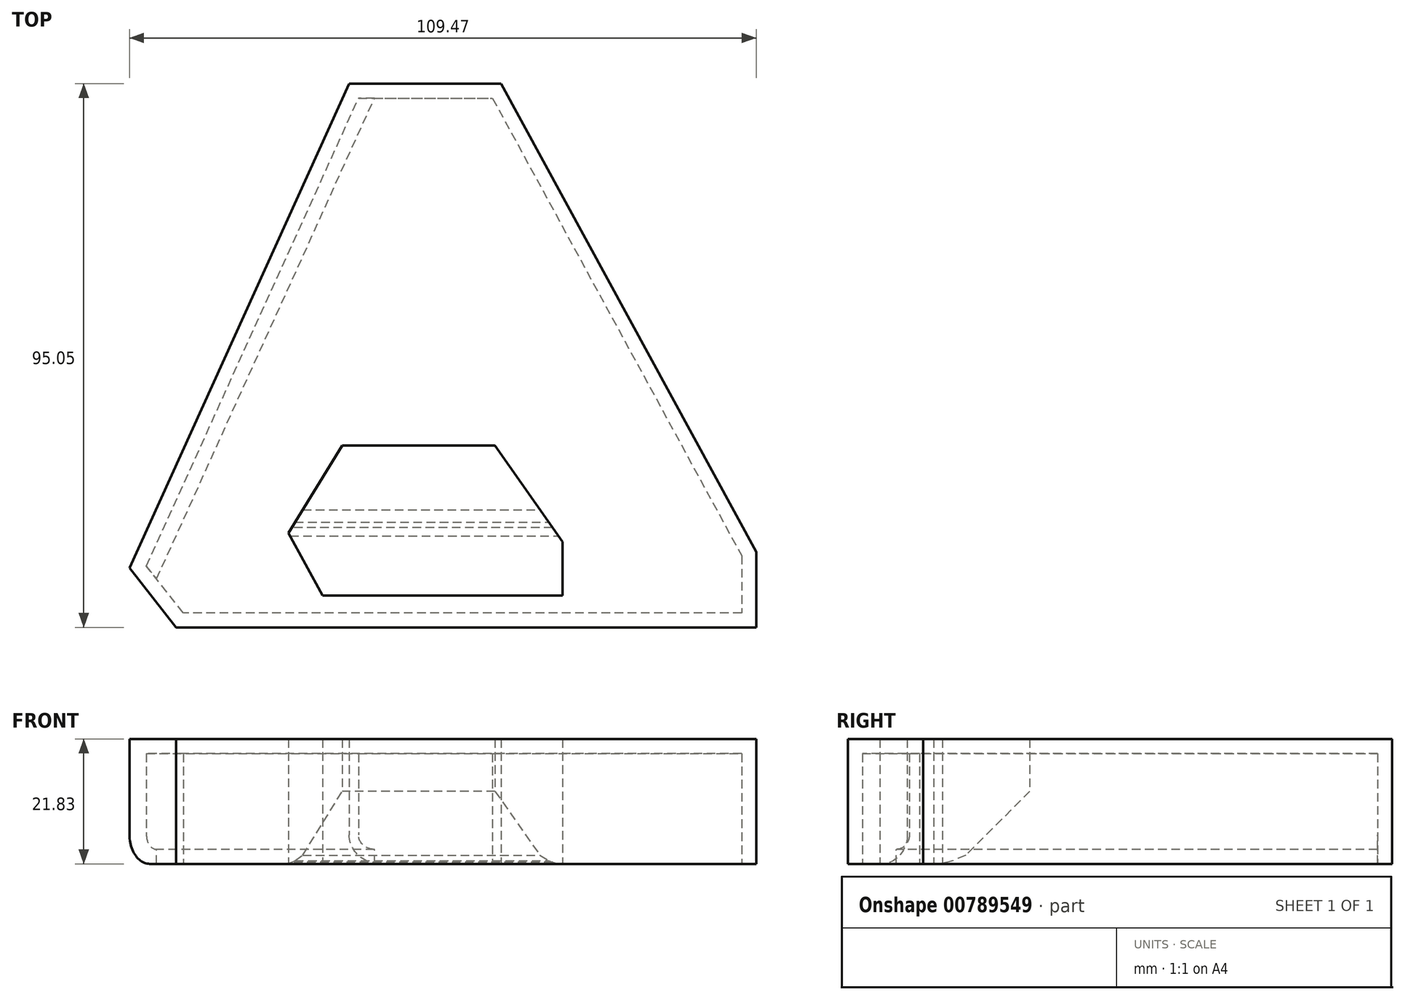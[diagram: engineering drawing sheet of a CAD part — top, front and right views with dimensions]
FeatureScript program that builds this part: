
annotation { "Feature Type Name" : "Feature", "Feature Type Description" : "" }
export const myFeature = defineFeature(function(context is Context, id is Id, definition is map)
    precondition{}
    {
        {
            var Q0;
            Q0=qCreatedBy(makeId("Top.planeOp"),FACE);
            var sketch = newSketch(context, id + "F0", { "sketchPlane" : qUnion([Q0])});
            skLineSegment(sketch, "E0", {"start": v(-11, 53.07) * mm, "end": v(15.55, 53.07) * mm});
            skLineSegment(sketch, "E1", {"start": v(15.55, 53.07) * mm, "end": v(60.1, -28.8) * mm});
            skLineSegment(sketch, "E2", {"start": v(60.1, -28.8) * mm, "end": v(60.1, -41.98) * mm});
            skLineSegment(sketch, "E3", {"start": v(60.1, -41.98) * mm, "end": v(-41.23, -41.98) * mm});
            skLineSegment(sketch, "E4", {"start": v(-41.23, -41.98) * mm, "end": v(-49.37, -31.59) * mm});
            skLineSegment(sketch, "E5", {"start": v(-49.37, -31.59) * mm, "end": v(-11, 53.07) * mm});
            skSolve(sketch);
        }
        {
            var Q0;
            Q0=qCreatedBy(makeId("Top.planeOp"),FACE);
            var sketch = newSketch(context, id + "F1", { "sketchPlane" : qUnion([Q0])});
            skLineSegment(sketch, "E6", {"start": v(-15.66, -36.38) * mm, "end": v(26.25, -36.38) * mm});
            skLineSegment(sketch, "E7", {"start": v(26.25, -36.38) * mm, "end": v(26.25, -26.99) * mm});
            skLineSegment(sketch, "E8", {"start": v(26.25, -26.99) * mm, "end": v(14.48, -10.19) * mm});
            skLineSegment(sketch, "E9", {"start": v(14.48, -10.19) * mm, "end": v(-12.2, -10.19) * mm});
            skLineSegment(sketch, "E10", {"start": v(-12.2, -10.19) * mm, "end": v(-21.63, -25.46) * mm});
            skLineSegment(sketch, "E11", {"start": v(-21.63, -25.46) * mm, "end": v(-15.66, -36.38) * mm});
            skSolve(sketch);
        }
        {
            var Q0;
            Q0=makeQuery(id+"F1.imprint","IMPRINT",FACE,{"disambiguationData":[TD([[makeQuery(id+"F1.imprint","IMPRINT",EDGE,{"derivedFrom":sQuery(id+"F1.wireOp",EDGE,"E6")}),1.0]])]});
            var Q1;
            Q1=makeQuery(id+"F0.imprint","IMPRINT",FACE,{"disambiguationData":[TD([[makeQuery(id+"F0.imprint","IMPRINT",EDGE,{"derivedFrom":sQuery(id+"F0.wireOp",EDGE,"E0")}),-1.0]])]});
            extrude(context, id + "F2", {"entities" : qUnion([Q0, Q1]), "depth" : 21.83 * mm, "offsetDistance" : 25.4 * mm});
        }
        {
            var Q0;
            Q0=makeQuery(id+"F2.opExtrude","CAP_EDGE",EDGE,{"disambiguationData":[OSD([sQuery(id+"F0.wireOp",EDGE,"E5")])],"isStart":true});
            fillet(context, id + "F3", {"entities" : qUnion([Q0]), "radius" : 5.08 * mm, "tangentPropagation" : true, "allowEdgeOverflow" : false});
        }
        {
            var Q0;
            Q0=makeQuery(id+"F2.opExtrude","CAP_FACE",FACE,{"disambiguationData":[OSD([sQuery(id+"F0.wireOp",EDGE,"E0"),sQuery(id+"F0.wireOp",EDGE,"E1"),sQuery(id+"F0.wireOp",EDGE,"E2"),sQuery(id+"F0.wireOp",EDGE,"E3"),sQuery(id+"F0.wireOp",EDGE,"E4"),sQuery(id+"F0.wireOp",EDGE,"E5")])],"isStart":true});
            shell(context, id + "F4", {"entities" : qUnion([Q0]), "thickness" : 2.54 * mm});
        }
        {
            var Q0;
            Q0=makeQuery(id+"F2.opExtrude","CAP_EDGE",EDGE,{"disambiguationData":[OSD([sQuery(id+"F1.wireOp",EDGE,"E9")])],"isStart":true});
            chamfer(context, id + "F5", {"entities" : qUnion([Q0]), "width" : 12.7 * mm, "tangentPropagation" : true});
        }
        {
            var Q0;
            {var subQ0=sQuery(id+"F1.wireOp",EDGE,"E9");Q0=makeQuery(id+"F5.opChamfer","BLEND_EDGE",EDGE,{"blendedFrom":[makeQuery(id+"F2.opExtrude","CAP_EDGE",EDGE,{"disambiguationData":[OSD([subQ0])],"isStart":true}),makeQuery(id+"F2.opExtrude","CAP_FACE",FACE,{"disambiguationData":[OSD([sQuery(id+"F1.wireOp",EDGE,"E6"),sQuery(id+"F1.wireOp",EDGE,"E7"),sQuery(id+"F1.wireOp",EDGE,"E8"),subQ0,sQuery(id+"F1.wireOp",EDGE,"E10"),sQuery(id+"F1.wireOp",EDGE,"E11")])],"isStart":true})],"blendedInto":[makeQuery(id+"F2.opExtrude","CAP_FACE",FACE,{"disambiguationData":[OSD([sQuery(id+"F1.wireOp",EDGE,"E6"),sQuery(id+"F1.wireOp",EDGE,"E7"),sQuery(id+"F1.wireOp",EDGE,"E8"),subQ0,sQuery(id+"F1.wireOp",EDGE,"E10"),sQuery(id+"F1.wireOp",EDGE,"E11")])],"isStart":true})]});}
            chamfer(context, id + "F6", {"entities" : qUnion([Q0]), "width" : 5.08 * mm, "tangentPropagation" : true});
        }
        {
            var Q0;
            {var subQ0=sQuery(id+"F1.wireOp",EDGE,"E9");var subQ1=makeQuery(id+"F2.opExtrude","CAP_FACE",FACE,{"disambiguationData":[OSD([sQuery(id+"F1.wireOp",EDGE,"E6"),sQuery(id+"F1.wireOp",EDGE,"E7"),sQuery(id+"F1.wireOp",EDGE,"E8"),subQ0,sQuery(id+"F1.wireOp",EDGE,"E10"),sQuery(id+"F1.wireOp",EDGE,"E11")])],"isStart":true});Q0=makeQuery(id+"F6.opChamfer","BLEND_EDGE",EDGE,{"blendedFrom":[makeQuery(id+"F5.opChamfer","BLEND_EDGE",EDGE,{"blendedFrom":[makeQuery(id+"F2.opExtrude","CAP_EDGE",EDGE,{"disambiguationData":[OSD([subQ0])],"isStart":true}),subQ1],"blendedInto":[subQ1]}),subQ1],"blendedInto":[subQ1]});}
            chamfer(context, id + "F7", {"entities" : qUnion([Q0]), "width" : 5.08 * mm, "tangentPropagation" : true});
        }
        {
            var Q0;
            {var subQ0=sQuery(id+"F1.wireOp",EDGE,"E11");var subQ1=sQuery(id+"F1.wireOp",EDGE,"E10");var subQ2=sQuery(id+"F1.wireOp",EDGE,"E9");var subQ3=sQuery(id+"F1.wireOp",EDGE,"E8");var subQ4=sQuery(id+"F1.wireOp",EDGE,"E7");var subQ5=sQuery(id+"F1.wireOp",EDGE,"E6");var subQ6=makeQuery(id+"F2.opExtrude","CAP_FACE",FACE,{"disambiguationData":[OSD([subQ5,subQ4,subQ3,subQ2,subQ1,subQ0])],"isStart":true});Q0=makeQuery(id+"F7.opChamfer","BLEND_EDGE",EDGE,{"blendedFrom":[makeQuery(id+"F6.opChamfer","BLEND_EDGE",EDGE,{"blendedFrom":[makeQuery(id+"F5.opChamfer","BLEND_EDGE",EDGE,{"blendedFrom":[makeQuery(id+"F2.opExtrude","CAP_EDGE",EDGE,{"disambiguationData":[OSD([subQ2])],"isStart":true}),subQ6],"blendedInto":[subQ6]}),subQ6],"blendedInto":[subQ6]}),makeQuery(id+"F6.opChamfer","BLEND_FACE",FACE,{"disambiguationData":[OSD([subQ5,subQ4,subQ3,subQ2,subQ1,subQ0])]})],"blendedInto":[makeQuery(id+"F6.opChamfer","BLEND_FACE",FACE,{"disambiguationData":[OSD([subQ5,subQ4,subQ3,subQ2,subQ1,subQ0])]})]});}
            chamfer(context, id + "F8", {"entities" : qUnion([Q0]), "width" : 5.08 * mm, "tangentPropagation" : true});
        }
    });
